# Revit family: Hager-Univers-IP44-D205-H1950-Cl.I-encl-NoHosted-NL-en
name_source: partatom
category: Equipement électrique
units: mm (PartAtom-declared; Revit-internal decimal feet)

## family parameters
Basée sur le plan de construction = Oui
Configuration du panneau = Deux colonnes, circuits au sein
Cote de connecteur circulaire = Utiliser le diamètre
Couper avec des vides une fois chargée = Non
Partagée = Non
Point de calcul de pièce = Non
Toujours verticalement = Oui
Type d'élément = Tableau de raccordement

## types (5) — shared parameters
Commentaires du type = Univers
EF000003 - Mounting method = EV012274 - Floor installation
EF000007 - Colour = EV000202 - White
EF000040 - Height = 1950 mm  [stored 6.39764 ft]
EF000049 - Depth = 205 mm  [stored 0.672572 ft]
EF000116 - RAL-number = 9010
EF000118 - With mounting plate = Non
EF000266 - Number of rows = 12
EF000339 - Type of cover = EV001012 - Cover
EF001088 - Extension possible = Oui
EF001131 - Internal depth = 205 mm  [stored 0.672572 ft]
EF001596 - Material housing = EV000179 - Steel
EF001613 - Circuit integrity = EV000494 - None
EF003532 - Suitable for outdoor use = Non
EF004293 - Impact strength = EV006815 - IK09
EF005474 - Degree of protection (IP) = EV006418 - IP44
EF006244 - Transparent cover/door = Non
EF006306 - With lock = Non
EF007800 - Suitable for lightning protection = Non
EF009170 - Material plate thickness cabinet = 1 mm  [stored 0.00328084 ft]
EF009171 - Material plate thickness door/cover = 1 mm  [stored 0.00328084 ft]
EF009212 - Cover model = EV000116 - Closed
EF015940 - Cover with overpressure release = Non
Elévation par défaut = 1219 mm
Fabricant = Hager
HG000002 - With door or cover = Oui
HG000003 - Range = Univers
HG000006 - Flush mounted = Non
HG000023 - Double section enclosure = Non
HG000024 - Bottom section height = 600 mm
HG000026 - Floor standing = Oui
HG000027 - Plinth height = 100 mm  [stored 0.328084 ft]
zero-valued in all types: EF000218 - Built-in depth

## per-type parameters (varying)
| type | EF000008 - Width | EF000437 - Number of conduit inlets | EF002950 - Width in number of modular spacings | EF004427 - Number of modules | EF004464 - Type of door | EF008873 - Nominal current (In) | EF009554 - Number of openings for flange plates | HG000004 - Manufacturer reference | HG000009 - Double swing door | HG000010 - Asymmetric doors |
| Floor installation IP44 W1050 H1950 D205  - FP24TN2 | 1050 mm | 8 | 48 | 576 | EV003602 - Double | 400 A | 8 | FP24TN2 | Oui | Non |
| Floor installation IP44 W1300 H1950 D205  - FP25TN2 | 1300 mm  [stored 4.26509 ft] | 10 | 60 | 720 | EV003602 - Double | 400 A | 10 | FP25TN2 | Oui | Oui |
| Floor installation IP44 W300 H1950 D205  - FP21TN2 | 300 mm | 2 | 12 | 144 | EV002646 - Single | 250 A | 2 | FP21TN2 | Non | Non |
| Floor installation IP44 W550 H1950 D205  - FP22TN2 | 550 mm | 4 | 24 | 288 | EV002646 - Single | 400 A | 4 | FP22TN2 | Non | Non |
| Floor installation IP44 W800 H1950 D205  - FP23TN2 | 800 mm  [stored 2.62467 ft] | 6 | 36 | 432 | EV002646 - Single | 400 A | 6 | FP23TN2 | Non | Non |

note: [stored X ft] marks values corroborated as IEEE doubles in the binary element streams (Revit-internal decimal feet)

## geometry (parser evidence)
native form markers: Blend x4, Sweep x11
no freeform markers — native parametric forms only
